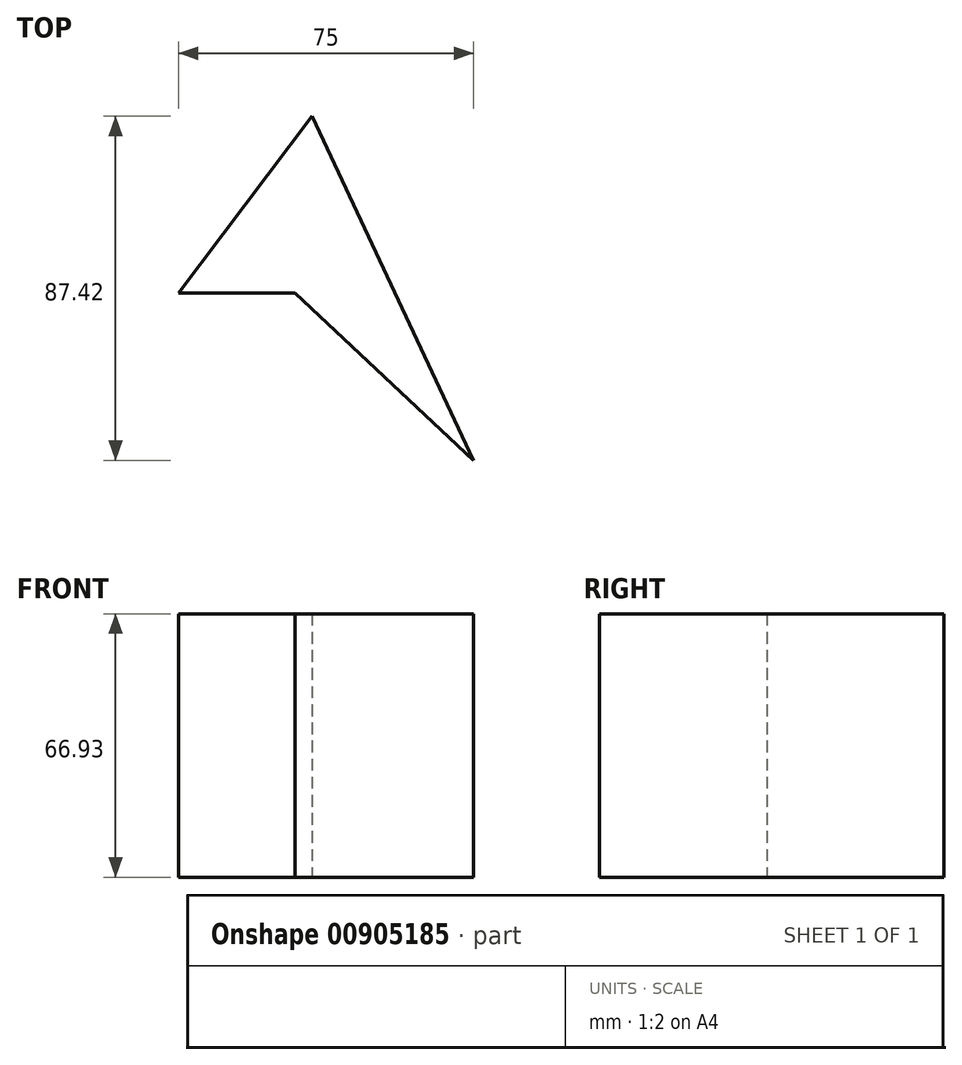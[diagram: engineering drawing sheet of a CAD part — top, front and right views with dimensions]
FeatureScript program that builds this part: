
annotation { "Feature Type Name" : "Feature", "Feature Type Description" : "" }
export const myFeature = defineFeature(function(context is Context, id is Id, definition is map)
    precondition{}
    {
        {
            var Q0;
            Q0=qCreatedBy(makeId("Top.planeOp"),FACE);
            var sketch = newSketch(context, id + "F0", { "sketchPlane" : qUnion([Q0])});
            skLineSegment(sketch, "E0", {"start": v(75, -75.15) * mm, "end": v(33.93, 12.27) * mm});
            skLineSegment(sketch, "E1", {"start": v(33.93, 12.27) * mm, "end": v(0, -32.64) * mm});
            skLineSegment(sketch, "E2", {"start": v(0, -32.64) * mm, "end": v(29.58, -32.64) * mm});
            skLineSegment(sketch, "E3", {"start": v(29.58, -32.64) * mm, "end": v(75, -75.15) * mm});
            skSolve(sketch);
        }
        {
            var Q0;
            Q0 = qSketchRegion(id + "F0", true);
            extrude(context, id + "F1", {"entities" : qUnion([Q0]), "depth" : 66.93 * mm, "offsetDistance" : 25.4 * mm});
        }
    });
